FCSTD DOCUMENT  (FreeCAD 1.1R38827 (Git))
Label: composit_stand3_basement_top_main
License: All rights reserved
LicenseURL: http://en.wikipedia.org/wiki/All_rights_reserved
objects: Sketcher::SketchObject×1
note: 2 computed .brp shape members not serialized (recipe doc carries the construction recipe); baked Part::Feature solids carry a one-line shape summary decoded from their .brp

FEATURE [Sketcher::SketchObject] Sketch  label="basement_top_main_sketch"
  ArcFitTolerance = 0
  FullyConstrained = true
  MakeInternals = false
  sketch-geometry (4):
    g0: LineSegment [constr] StartX=0 StartY=0 StartZ=0 EndX=126.5 EndY=219.104 EndZ=0
    g1: ArcOfCircle CenterX=0 CenterY=0 CenterZ=0 NormalX=0 NormalY=0 NormalZ=1 AngleXU=0 Radius=349.171 StartAngle=0 EndAngle=0.0396574
    g2: ArcOfCircle CenterX=302.433 CenterY=12 CenterZ=0 NormalX=0 NormalY=0 NormalZ=1 AngleXU=0 Radius=46.5 StartAngle=0.0396574 EndAngle=0.699903
    g3: ArcOfCircle CenterX=-272.703 CenterY=-472.335 CenterZ=0 NormalX=0 NormalY=0 NormalZ=1 AngleXU=0 Radius=798.406 StartAngle=0.699903 EndAngle=1.0472
  constraints (12):
    c: Coincident(g0,g-1)
    c: Angle(g0) = 1.0472
    c: Coincident(g1,g0)
    c: PointOnObject(g1,g-1)
    c: Coincident(g3,g0)
    c: Tangent(g2,g1) = -1.5708
    c: Tangent(g3,g2) = -1.5708
    c: Perpendicular(g3,g0)
    c: DistanceX(g1) = 349.171  'max_r'
    c: Distance(g0) = 253  'min_r'
    c: Radius(g2) = 46.5
    c: DistanceY(g2) = 12
